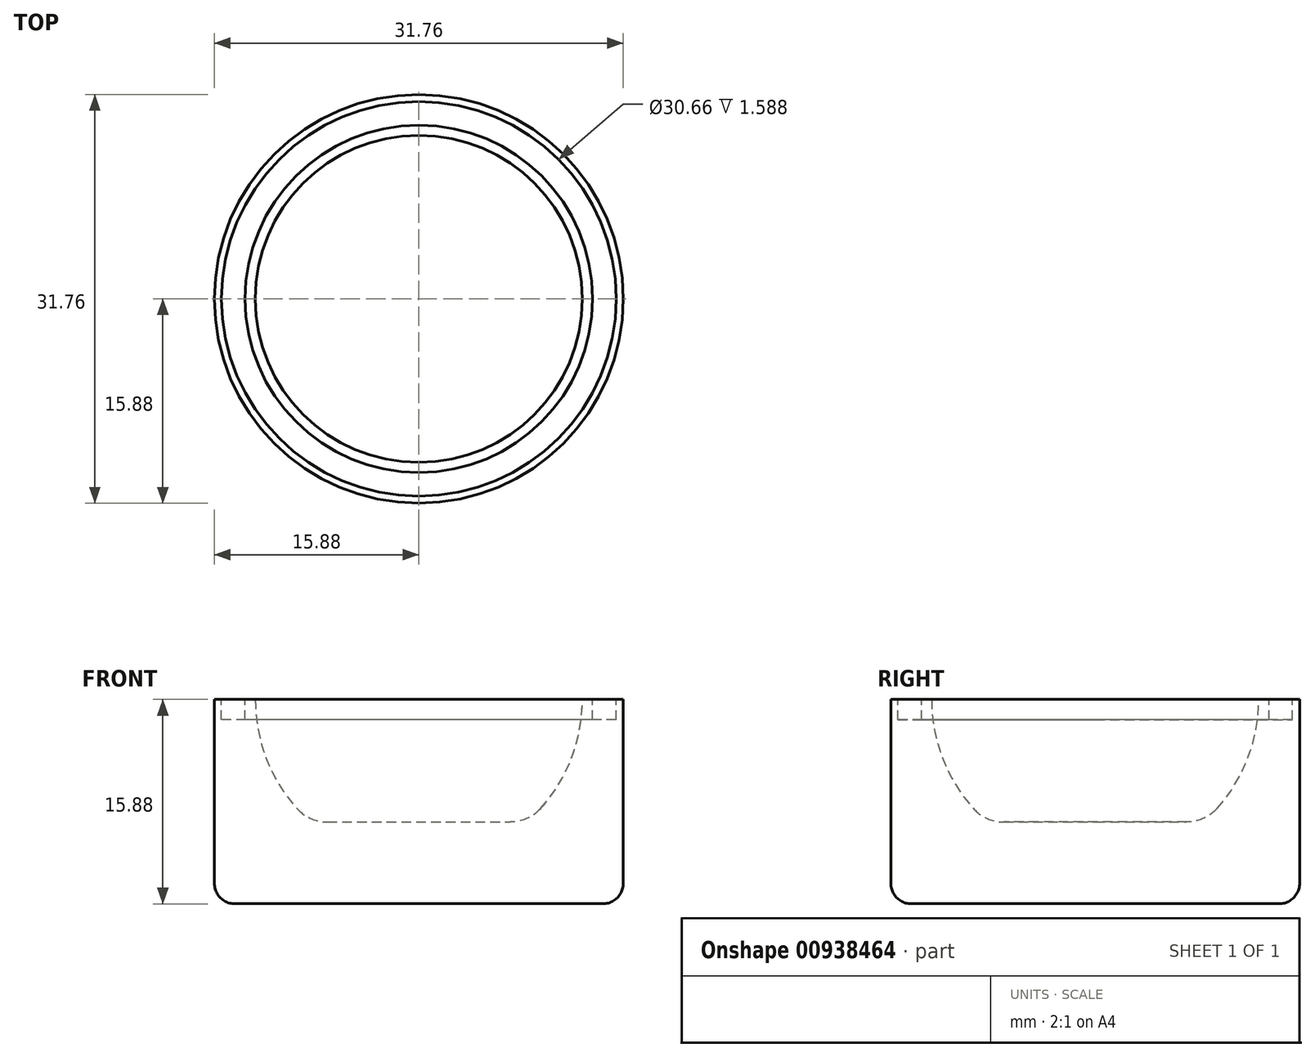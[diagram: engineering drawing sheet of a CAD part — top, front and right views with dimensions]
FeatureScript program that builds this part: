
annotation { "Feature Type Name" : "Feature", "Feature Type Description" : "" }
export const myFeature = defineFeature(function(context is Context, id is Id, definition is map)
    precondition{}
    {
        {
            var Q0;
            Q0=qCreatedBy(makeId("Front.planeOp"),FACE);
            var sketch = newSketch(context, id + "F0", { "sketchPlane" : qUnion([Q0])});
            skLineSegment(sketch, "E0.bottom", {"start": v(-15.88, 0) * mm, "end": v(15.88, 0) * mm});
            skLineSegment(sketch, "E0.top", {"start": v(-15.88, -15.87) * mm, "end": v(15.88, -15.87) * mm});
            skLineSegment(sketch, "E0.left", {"start": v(-15.88, 0) * mm, "end": v(-15.88, -15.87) * mm});
            skLineSegment(sketch, "E0.right", {"start": v(15.88, 0) * mm, "end": v(15.88, -15.87) * mm});
            skCircle(sketch, "E1", {"center": v(0, 0) * mm, "radius": 12.7 * mm});
            skLineSegment(sketch, "E2", {"start": v(0, 29.66) * mm, "end": v(0, -32.53) * mm});
            skSolve(sketch);
        }
        {
            var Q0;
            {var subQ0=sQuery(id+"F0.wireOp",EDGE,"E0.left");Q0=makeQuery(id+"F0.imprint","IMPRINT",FACE,{"disambiguationData":[TD([[makeQuery(id+"F0.imprint","IMPRINT",EDGE,{"derivedFrom":subQ0}),1.0]])]});}
            var Q1;
            Q1=sQuery(id+"F0.wireOp",EDGE,"E2");
            revolve(context, id + "F1", {"surfaceOperationType" : NewSurfaceOperationType.NEW, "entities" : qUnion([Q0]), "axis" : qUnion([Q1]), "revolveType" : RevolveType.ONE_DIRECTION, "angle" : 360 * degree});
        }
        {
            var Q0;
            Q0=makeQuery(id+"F1.opRevolve","SWEPT_FACE",FACE,{"disambiguationData":[OSD([sQuery(id+"F0.wireOp",EDGE,"E0.top")])]});
            extrude(context, id + "F2", {"entities" : qUnion([Q0]), "operationType" : NewBodyOperationType.ADD, "oppositeDirection" : true, "depth" : 6.35 * mm, "offsetDistance" : 25.4 * mm});
        }
        {
            var Q0;
            Q0=makeQuery(id+"F2.boolean.opBoolean","INTERSECT",EDGE,{"derivedFrom":[makeQuery(id+"F1.opRevolve","SWEPT_FACE",FACE,{"disambiguationData":[OSD([sQuery(id+"F0.wireOp",EDGE,"E1")])]}),makeQuery(id+"F2.opExtrude","CAP_FACE",FACE,{"disambiguationData":[OSD([sQuery(id+"F0.wireOp",EDGE,"E0.top")])],"isStart":false})]});
            fillet(context, id + "F3", {"entities" : qUnion([Q0]), "radius" : 3.17 * mm, "tangentPropagation" : true, "allowEdgeOverflow" : false});
        }
        {
            var Q0;
            Q0=makeQuery(id+"F1.opRevolve","SWEPT_FACE",FACE,{"disambiguationData":[OSD([sQuery(id+"F0.wireOp",EDGE,"E0.bottom")])]});
            var sketch = newSketch(context, id + "F4", { "sketchPlane" : qUnion([Q0])});
            skCircle(sketch, "E3", {"center": v(0, 0) * mm, "radius": 13.5 * mm});
            skCircle(sketch, "E4", {"center": v(0, 0) * mm, "radius": 15.33 * mm});
            skSolve(sketch);
        }
        {
            var Q0;
            Q0 = qSketchRegion(id + "F4", true);
            extrude(context, id + "F5", {"entities" : qUnion([Q0]), "operationType" : NewBodyOperationType.REMOVE, "oppositeDirection" : true, "depth" : 1.59 * mm, "offsetDistance" : 25.4 * mm});
        }
        {
            var Q0;
            Q0=makeQuery(id+"F1.opRevolve","SWEPT_EDGE",EDGE,{"disambiguationData":[OSD([sQuery(id+"F0.wireOp",EDGE,"E0.top"),sQuery(id+"F0.wireOp",EDGE,"E0.left")])]});
            fillet(context, id + "F6", {"entities" : qUnion([Q0]), "radius" : 1.59 * mm, "tangentPropagation" : true, "allowEdgeOverflow" : false});
        }
    });
